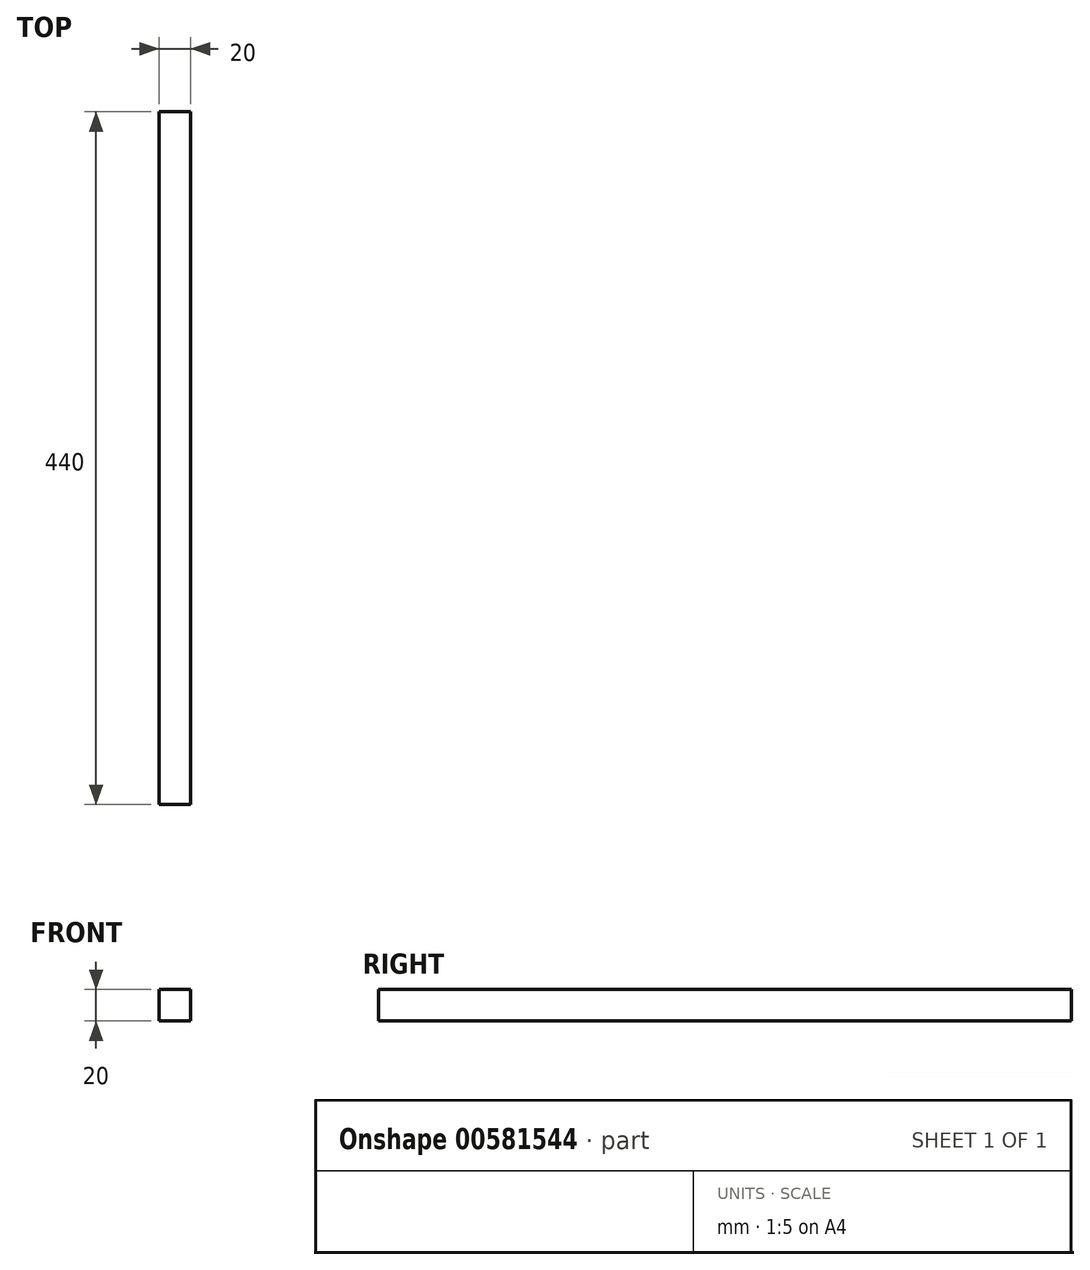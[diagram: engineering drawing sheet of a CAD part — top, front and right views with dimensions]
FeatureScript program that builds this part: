
annotation { "Feature Type Name" : "Feature", "Feature Type Description" : "" }
export const myFeature = defineFeature(function(context is Context, id is Id, definition is map)
    precondition{}
    {
        {
            var Q0;
            Q0=qCreatedBy(makeId("Front.planeOp"),FACE);
            var sketch = newSketch(context, id + "F0", { "sketchPlane" : qUnion([Q0])});
            skLineSegment(sketch, "E0.bottom", {"start": v(0, 0) * mm, "end": v(20, 0) * mm});
            skLineSegment(sketch, "E0.top", {"start": v(0, 20) * mm, "end": v(20, 20) * mm});
            skLineSegment(sketch, "E0.left", {"start": v(0, 0) * mm, "end": v(0, 20) * mm});
            skLineSegment(sketch, "E0.right", {"start": v(20, 0) * mm, "end": v(20, 20) * mm});
            skSolve(sketch);
        }
        {
            var Q0;
            Q0=makeQuery(id+"F0.imprint","IMPRINT",FACE,{"disambiguationData":[TD([[makeQuery(id+"F0.imprint","IMPRINT",EDGE,{"derivedFrom":sQuery(id+"F0.wireOp",EDGE,"E0.bottom")}),1.0]])]});
            extrude(context, id + "F1", {"entities" : qUnion([Q0]), "depth" : 440 * mm, "offsetDistance" : 25 * mm});
        }
    });
